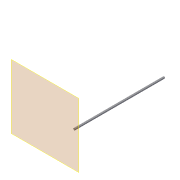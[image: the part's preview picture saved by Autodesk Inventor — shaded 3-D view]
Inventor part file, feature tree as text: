
AUTODESK INVENTOR PART (.ipt)
format: ipt  version: 2016 (Build 200138000, 138)  size: 86,016 bytes
history: native  units: in
note: dims shown in document units (in); Inventor stores cm internally (conversion verified against a paired STEP export)
features: reference x4, extrude x2, plane x1, sketch x1, projected_geometry x1
ambient origin geometry x8: Origin, YZ Plane, XZ Plane, XY Plane, X Axis, Y Axis, Z Axis, Center Point
bodies: Solid1 (feature_tree)
feature tree (9):
  plane  "Work Plane1"
  extrude  "Extrusion1"  Depth=0.0394in
  extrude  "Extrusion2"  Depth=0.0394in TaperAngle=0.0deg
  reference  "Reference5"
  reference  "Reference6"
  reference  "Reference7"
  reference  "Reference8"
  sketch  "Sketch2"  dims[d0=21.6535in d1=0.0in d2=0.0394in d3=23.2283in d4=0.0in]
  projected_geometry  "Projected Loop1"
